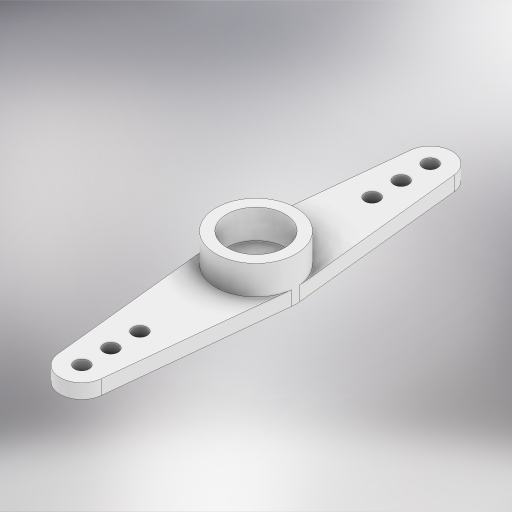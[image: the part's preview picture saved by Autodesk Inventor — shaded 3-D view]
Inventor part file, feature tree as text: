
AUTODESK INVENTOR PART (.ipt)
format: ipt  version: 2024 (Build 280153000, 153)  size: 359,424 bytes
history: native  units: in
note: dims shown in document units (in); Inventor stores cm internally (conversion verified against a paired STEP export)
features: extrude x3, sketch x3, projected_geometry x1
ambient origin geometry x8: Origin, YZ Plane, XZ Plane, XY Plane, X Axis, Y Axis, Z Axis, Center Point
bodies: Solid1 (feature_tree)
feature tree (7):
  extrude  "Extrusion1"  Depth=0.1181in
  extrude  "Extrusion2"  Depth=0.0394in TaperAngle=0.0deg
  extrude  "Extrusion3"  Depth=0.0394in
  sketch  "Sketch1"  dims[d0=0.2165in d1=0.1181in]
  sketch  "Sketch2"  dims[d2=1.063in d3=0.0394in d4=0.0in]
  sketch  "Sketch3"  dims[d5=0.2165in d6=0.1575in d7=0.0787in d8=0.0in d9=0.0394in d10=0.0394in d11=0.0394in d12=0.0394in d13=0.0394in d14=0.7874in d16=180.0deg d18=0.0in d19=0.0in]
  projected_geometry  "Projected Loop1"
